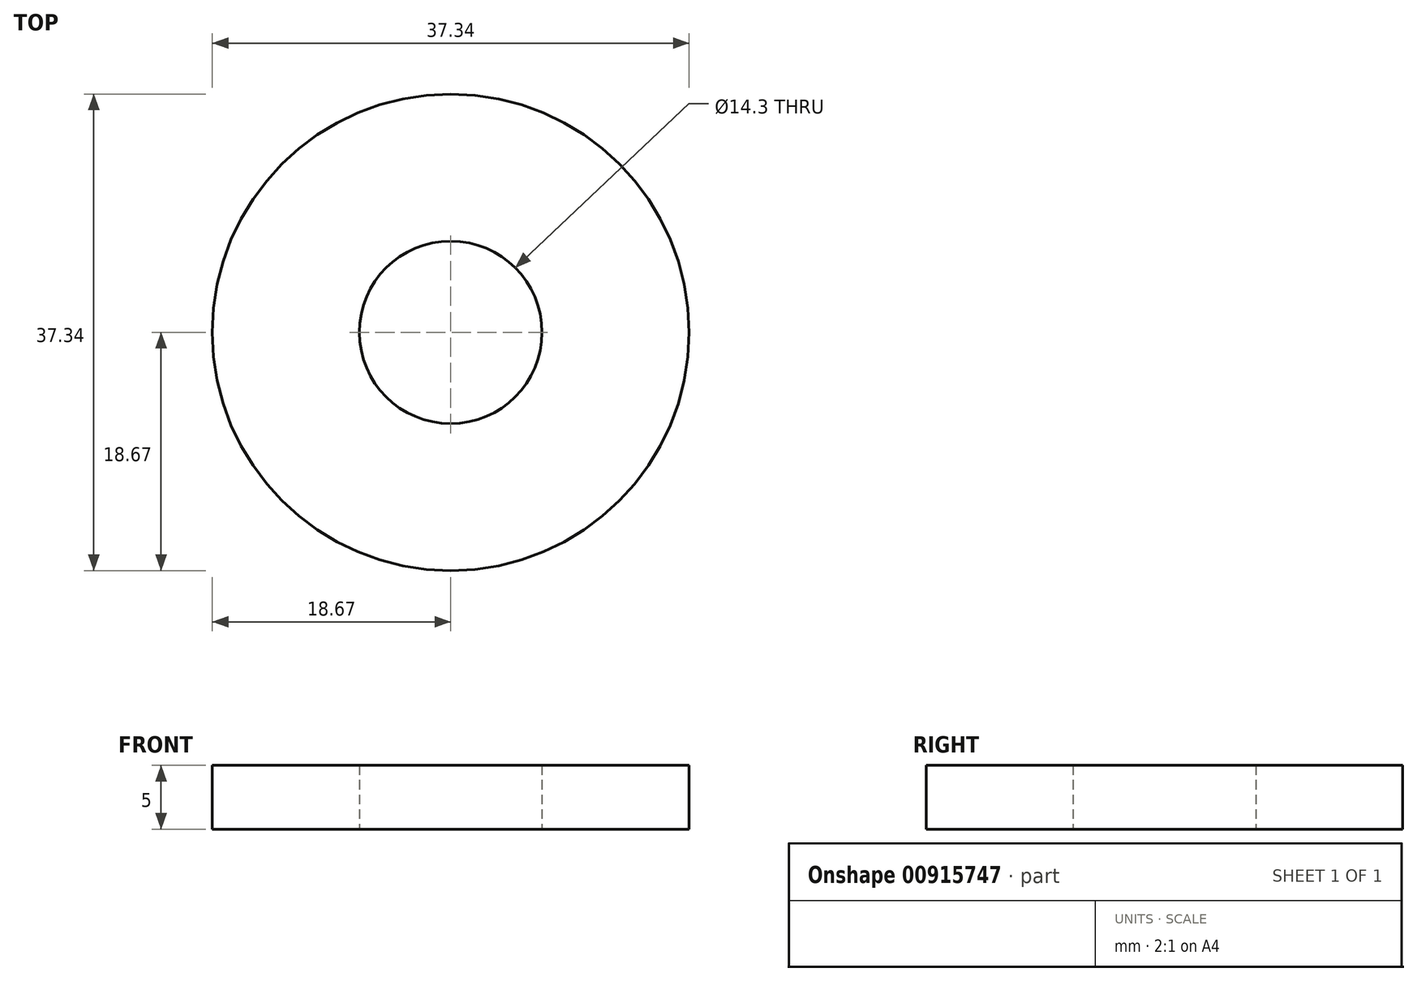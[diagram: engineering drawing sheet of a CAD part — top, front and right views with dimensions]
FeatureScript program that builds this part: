
annotation { "Feature Type Name" : "Feature", "Feature Type Description" : "" }
export const myFeature = defineFeature(function(context is Context, id is Id, definition is map)
    precondition{}
    {
        {
            var Q0;
            Q0=qCreatedBy(makeId("Top.planeOp"),FACE);
            var sketch = newSketch(context, id + "F0", { "sketchPlane" : qUnion([Q0])});
            skCircle(sketch, "E0", {"center": v(0, 0) * mm, "radius": 18.67 * mm});
            skCircle(sketch, "E1", {"center": v(0, 0) * mm, "radius": 7.15 * mm});
            skSolve(sketch);
        }
        {
            var Q0;
            Q0=makeQuery(id+"F0.imprint","IMPRINT",FACE,{"disambiguationData":[TD([[makeQuery(id+"F0.imprint","IMPRINT",EDGE,{"derivedFrom":sQuery(id+"F0.wireOp",EDGE,"E0")}),1.0]])]});
            extrude(context, id + "F1", {"entities" : qUnion([Q0]), "depth" : 5 * mm, "offsetDistance" : 25.4 * mm});
        }
    });
